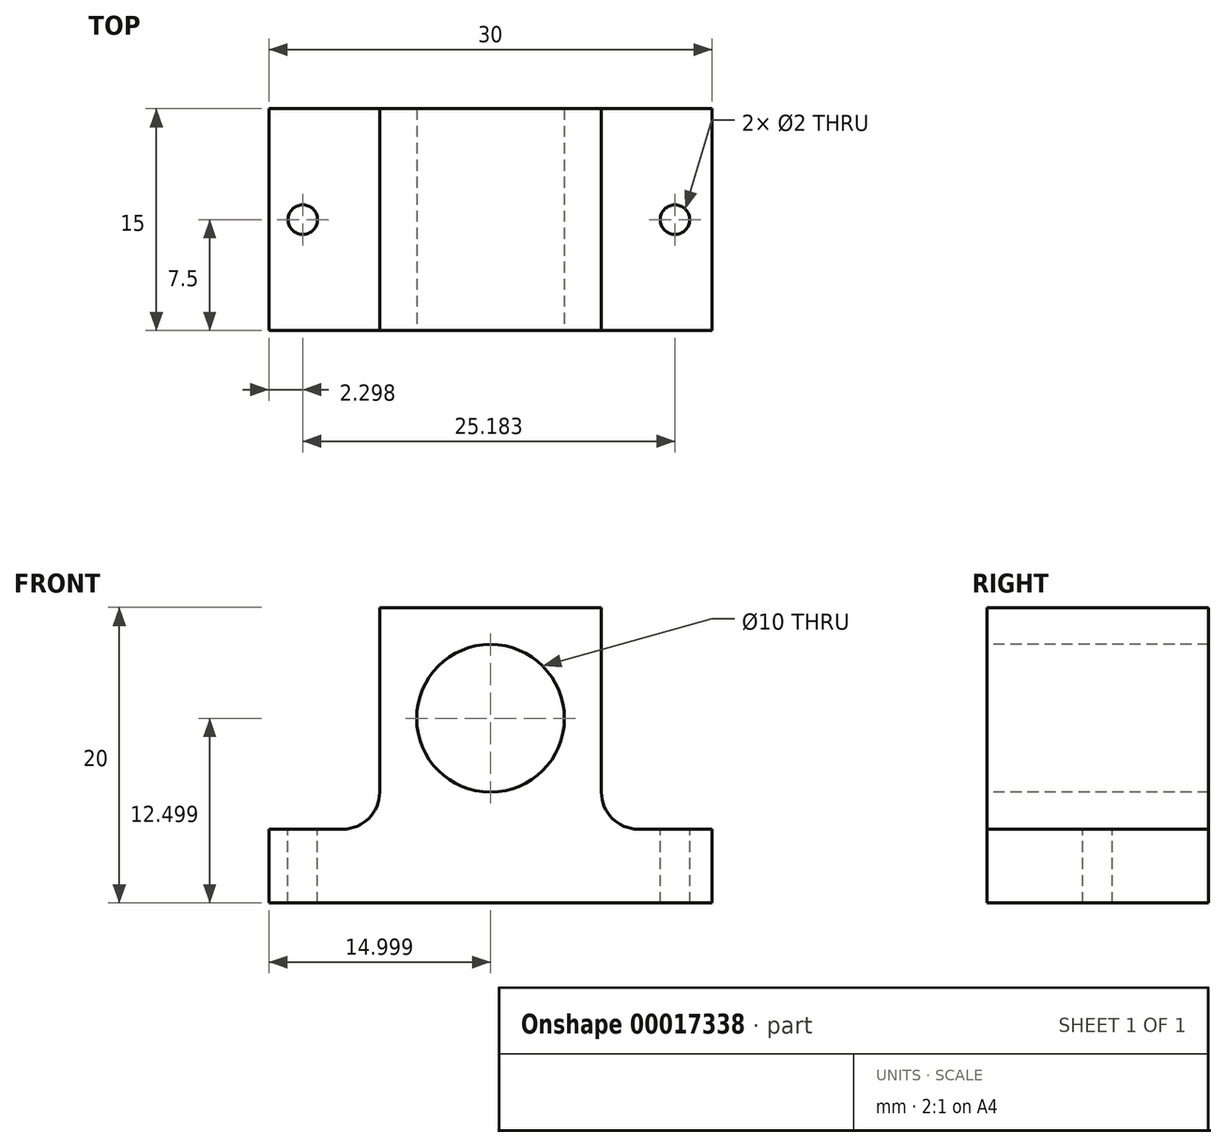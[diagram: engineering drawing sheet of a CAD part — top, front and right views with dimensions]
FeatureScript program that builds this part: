
annotation { "Feature Type Name" : "Feature", "Feature Type Description" : "" }
export const myFeature = defineFeature(function(context is Context, id is Id, definition is map)
    precondition{}
    {
        {
            var Q0;
            Q0=qCreatedBy(makeId("Front.planeOp"),FACE);
            var sketch = newSketch(context, id + "F0", { "sketchPlane" : qUnion([Q0])});
            skLineSegment(sketch, "E0", {"start": v(-24.58, -14.48) * mm, "end": v(-24.58, -9.48) * mm});
            skLineSegment(sketch, "E1", {"start": v(-24.58, -9.48) * mm, "end": v(-19.58, -9.48) * mm});
            skLineSegment(sketch, "E2", {"start": v(-17.08, -6.98) * mm, "end": v(-17.08, 5.52) * mm});
            skLineSegment(sketch, "E3", {"start": v(-17.08, 5.52) * mm, "end": v(-2.08, 5.52) * mm});
            skLineSegment(sketch, "E4", {"start": v(-2.08, 5.52) * mm, "end": v(-2.08, -6.98) * mm});
            skLineSegment(sketch, "E5", {"start": v(0.42, -9.48) * mm, "end": v(5.42, -9.48) * mm});
            skLineSegment(sketch, "E6", {"start": v(5.42, -9.48) * mm, "end": v(5.42, -14.48) * mm});
            skLineSegment(sketch, "E7", {"start": v(5.42, -14.48) * mm, "end": v(-24.58, -14.48) * mm});
            skPoint(sketch, "E8.visualSharp", {"position": v(-17.08, -9.48) * mm});
            skArc(sketch, "E8.filletArc", {"start": v(-19.58, -9.48) * mm, "mid": v(-17.81, -8.75) * mm, "end": v(-17.08, -6.98) * mm});
            skPoint(sketch, "E9.visualSharp", {"position": v(-2.08, -9.48) * mm});
            skArc(sketch, "E9.filletArc", {"start": v(-2.08, -6.98) * mm, "mid": v(-1.35, -8.75) * mm, "end": v(0.42, -9.48) * mm});
            skSolve(sketch);
        }
        {
            var Q0;
            Q0=makeQuery(id+"F0.imprint","IMPRINT",FACE,{"disambiguationData":[TD([[makeQuery(id+"F0.imprint","IMPRINT",EDGE,{"derivedFrom":sQuery(id+"F0.wireOp",EDGE,"E0")}),-1.0]])]});
            extrude(context, id + "F1", {"entities" : qUnion([Q0]), "depth" : 15 * mm});
        }
        {
            var Q0;
            Q0=makeQuery(id+"F1.opExtrude","SWEPT_FACE",FACE,{"disambiguationData":[OSD([sQuery(id+"F0.wireOp",EDGE,"E1")])]});
            var sketch = newSketch(context, id + "F2", { "sketchPlane" : qUnion([Q0])});
            skCircle(sketch, "E10", {"center": v(-22.28, -7.5) * mm, "radius": 1 * mm});
            skSolve(sketch);
        }
        {
            var Q0;
            Q0=makeQuery(id+"F2.imprint","IMPRINT",FACE,{"disambiguationData":[TD([[makeQuery(id+"F2.imprint","IMPRINT",EDGE,{"derivedFrom":sQuery(id+"F2.wireOp",EDGE,"E10")}),1.0]])]});
            extrude(context, id + "F3", {"entities" : qUnion([Q0]), "operationType" : NewBodyOperationType.REMOVE, "oppositeDirection" : true, "depth" : 25 * mm});
        }
        {
            var Q0;
            Q0=makeQuery(id+"F1.opExtrude","SWEPT_FACE",FACE,{"disambiguationData":[OSD([sQuery(id+"F0.wireOp",EDGE,"E5")])]});
            var sketch = newSketch(context, id + "F4", { "sketchPlane" : qUnion([Q0])});
            skCircle(sketch, "E11", {"center": v(2.9, -7.5) * mm, "radius": 1 * mm});
            skSolve(sketch);
        }
        {
            var Q0;
            Q0=makeQuery(id+"F4.imprint","IMPRINT",FACE,{"disambiguationData":[TD([[makeQuery(id+"F4.imprint","IMPRINT",EDGE,{"derivedFrom":sQuery(id+"F4.wireOp",EDGE,"E11")}),1.0]])]});
            extrude(context, id + "F5", {"entities" : qUnion([Q0]), "operationType" : NewBodyOperationType.REMOVE, "oppositeDirection" : true, "depth" : 25 * mm});
        }
        {
            var Q0;
            Q0=makeQuery(id+"F1.opExtrude","CAP_FACE",FACE,{"disambiguationData":[OSD([sQuery(id+"F0.wireOp",EDGE,"E0"),sQuery(id+"F0.wireOp",EDGE,"E1"),sQuery(id+"F0.wireOp",EDGE,"E2"),sQuery(id+"F0.wireOp",EDGE,"E3"),sQuery(id+"F0.wireOp",EDGE,"E4"),sQuery(id+"F0.wireOp",EDGE,"E5"),sQuery(id+"F0.wireOp",EDGE,"E6"),sQuery(id+"F0.wireOp",EDGE,"E7"),sQuery(id+"F0.wireOp",EDGE,"E8.filletArc"),sQuery(id+"F0.wireOp",EDGE,"E9.filletArc")])],"isStart":false});
            var sketch = newSketch(context, id + "F6", { "sketchPlane" : qUnion([Q0])});
            skCircle(sketch, "E12", {"center": v(-9.58, -1.98) * mm, "radius": 5 * mm});
            skSolve(sketch);
        }
        {
            var Q0;
            Q0=makeQuery(id+"F6.imprint","IMPRINT",FACE,{"disambiguationData":[TD([[makeQuery(id+"F6.imprint","IMPRINT",EDGE,{"derivedFrom":sQuery(id+"F6.wireOp",EDGE,"E12")}),1.0]])]});
            extrude(context, id + "F7", {"entities" : qUnion([Q0]), "operationType" : NewBodyOperationType.REMOVE, "oppositeDirection" : true, "depth" : 25 * mm});
        }
    });
